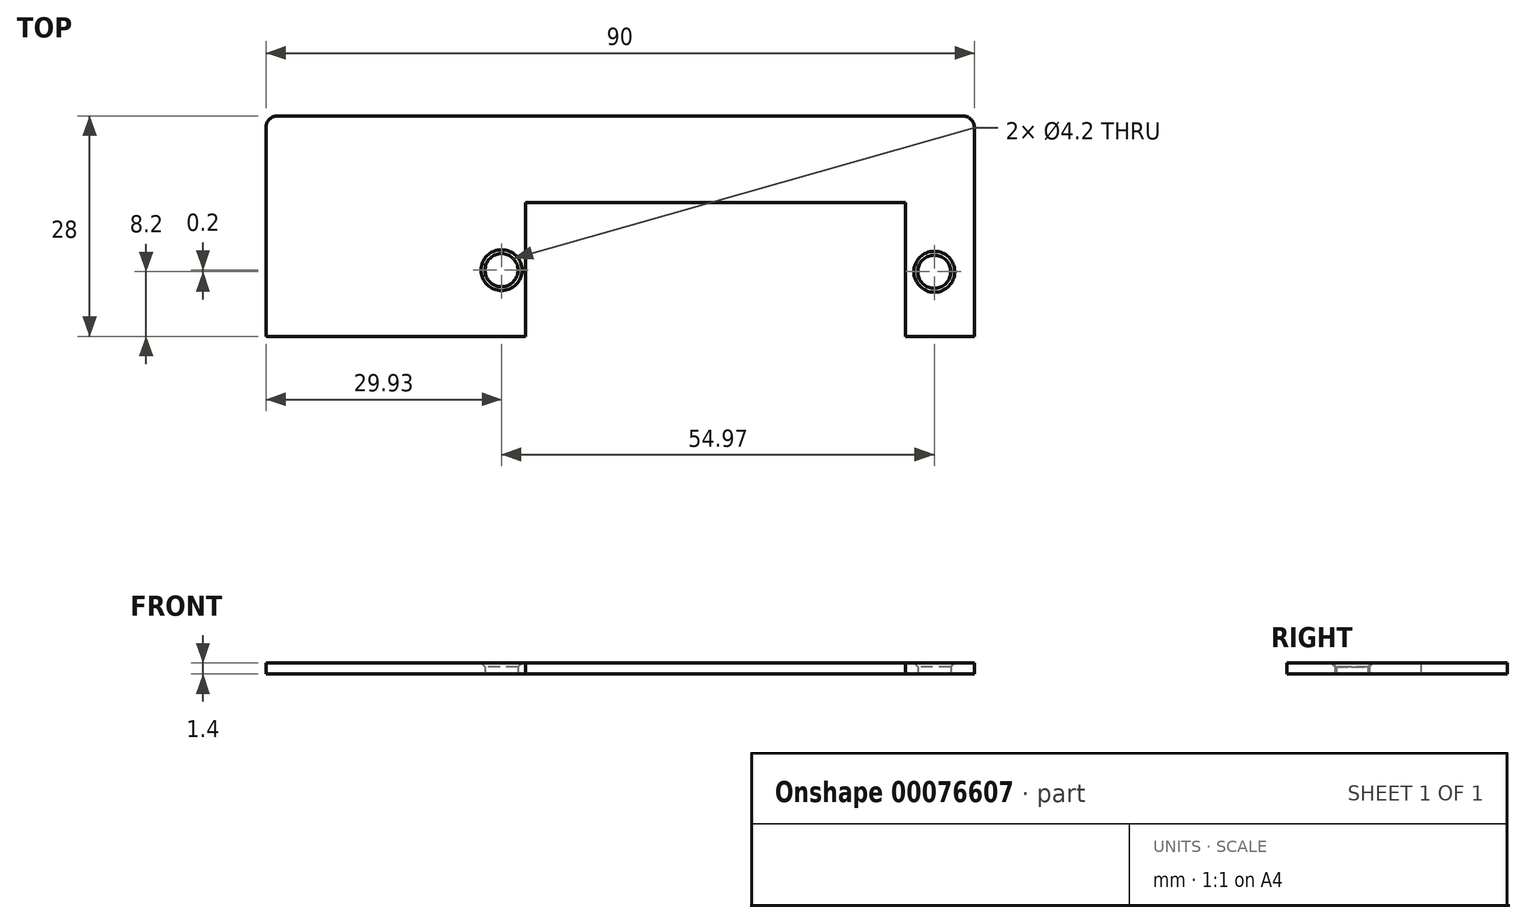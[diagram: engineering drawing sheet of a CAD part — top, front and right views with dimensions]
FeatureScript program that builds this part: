
annotation { "Feature Type Name" : "Feature", "Feature Type Description" : "" }
export const myFeature = defineFeature(function(context is Context, id is Id, definition is map)
    precondition{}
    {
        {
            var Q0;
            Q0=qCreatedBy(makeId("Top.planeOp"),FACE);
            var sketch = newSketch(context, id + "F0", { "sketchPlane" : qUnion([Q0])});
            skLineSegment(sketch, "E0.bottom", {"start": v(1.5, 0) * mm, "end": v(88.5, 0) * mm});
            skLineSegment(sketch, "E0.top", {"start": v(0, -28) * mm, "end": v(33, -28) * mm});
            skLineSegment(sketch, "E0.left", {"start": v(0, -1.5) * mm, "end": v(0, -28) * mm});
            skLineSegment(sketch, "E0.right", {"start": v(90, -1.5) * mm, "end": v(90, -28) * mm});
            skLineSegment(sketch, "E1", {"start": v(33, -28) * mm, "end": v(33, -11) * mm});
            skLineSegment(sketch, "E2", {"start": v(33, -11) * mm, "end": v(81.25, -11) * mm});
            skLineSegment(sketch, "E3", {"start": v(81.25, -11) * mm, "end": v(81.25, -28) * mm});
            skLineSegment(sketch, "E4.trimOffspring", {"start": v(81.25, -28) * mm, "end": v(90, -28) * mm});
            skLineSegment(sketch, "E5", {"start": v(0, -19.6) * mm, "end": v(29.93, -19.6) * mm, "construction": true});
            skLineSegment(sketch, "E6", {"start": v(29.93, -19.6) * mm, "end": v(29.93, -28) * mm, "construction": true});
            skLineSegment(sketch, "E7", {"start": v(90, -19.8) * mm, "end": v(84.9, -19.8) * mm, "construction": true});
            skLineSegment(sketch, "E8", {"start": v(84.9, -19.8) * mm, "end": v(84.9, -28) * mm, "construction": true});
            skCircle(sketch, "E9", {"center": v(29.93, -19.6) * mm, "radius": 2.1 * mm});
            skCircle(sketch, "E10", {"center": v(84.9, -19.8) * mm, "radius": 2.1 * mm});
            skPoint(sketch, "E11.visualSharp", {"position": v(0, 0) * mm});
            skArc(sketch, "E11.filletArc", {"start": v(1.5, 0) * mm, "mid": v(0.44, -0.44) * mm, "end": v(0, -1.5) * mm});
            skPoint(sketch, "E12.visualSharp", {"position": v(90, 0) * mm});
            skArc(sketch, "E12.filletArc", {"start": v(90, -1.5) * mm, "mid": v(89.56, -0.44) * mm, "end": v(88.5, 0) * mm});
            skSolve(sketch);
        }
        {
            var Q0;
            Q0=makeQuery(id+"F0.imprint","IMPRINT",FACE,{"disambiguationData":[TD([[makeQuery(id+"F0.imprint","IMPRINT",EDGE,{"derivedFrom":sQuery(id+"F0.wireOp",EDGE,"E0.bottom")}),-1.0]])]});
            extrude(context, id + "F1", {"entities" : qUnion([Q0]), "depth" : 1.4 * mm});
        }
        {
            var Q0;
            Q0=makeQuery(id+"F1.opExtrude","CAP_EDGE",EDGE,{"disambiguationData":[OSD([sQuery(id+"F0.wireOp",EDGE,"E9")])],"isStart":false});
            var Q1;
            Q1=makeQuery(id+"F1.opExtrude","CAP_EDGE",EDGE,{"disambiguationData":[OSD([sQuery(id+"F0.wireOp",EDGE,"E10")])],"isStart":false});
            chamfer(context, id + "F2", {"entities" : qUnion([Q0, Q1]), "width" : 0.5 * mm, "tangentPropagation" : true});
        }
    });
